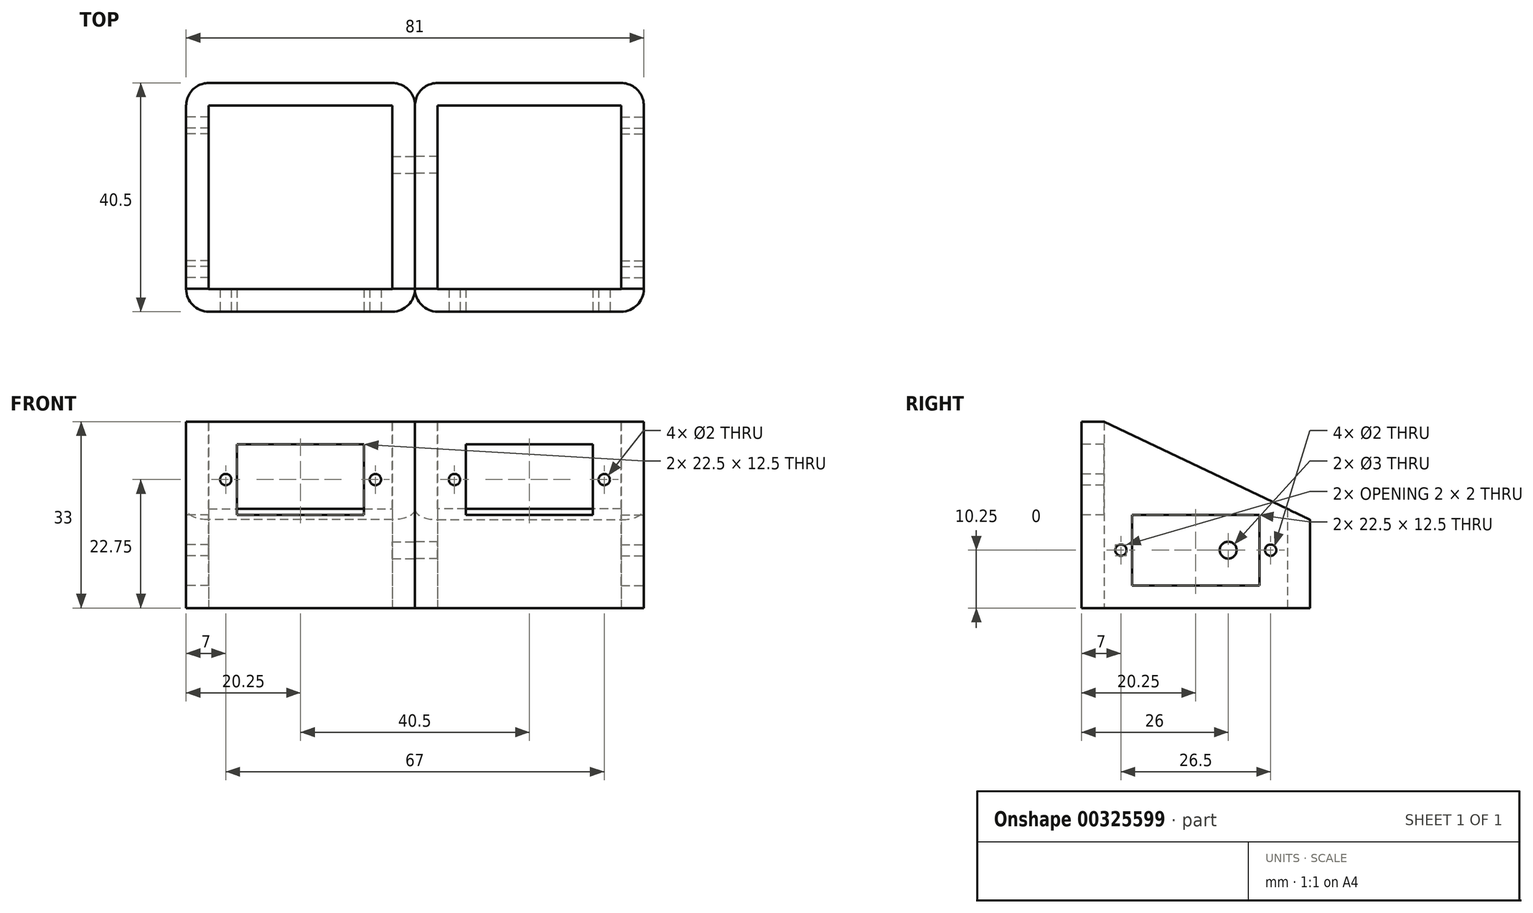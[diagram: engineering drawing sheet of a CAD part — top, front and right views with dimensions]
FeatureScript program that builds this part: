
annotation { "Feature Type Name" : "Feature", "Feature Type Description" : "" }
export const myFeature = defineFeature(function(context is Context, id is Id, definition is map)
    precondition{}
    {
        {
            assignVariable(context, id + "F0", {"name" : "s_w", "anyValue" : 12.5});
        }
        {
            assignVariable(context, id + "F1", {"name" : "size", "anyValue" : 4});
        }
        {
            var Q0;
            Q0=qCreatedBy(makeId("Top.planeOp"),FACE);
            var sketch = newSketch(context, id + "F2", { "sketchPlane" : qUnion([Q0])});
            skLineSegment(sketch, "E0.bottom", {"start": v(-20.25, 20.25) * mm, "end": v(20.25, 20.25) * mm});
            skLineSegment(sketch, "E0.top", {"start": v(-20.25, -20.25) * mm, "end": v(20.25, -20.25) * mm});
            skLineSegment(sketch, "E0.left", {"start": v(-20.25, 20.25) * mm, "end": v(-20.25, -20.25) * mm});
            skLineSegment(sketch, "E0.right", {"start": v(20.25, 20.25) * mm, "end": v(20.25, -20.25) * mm});
            skPoint(sketch, "E1", {"position": v(0, 20.25) * mm});
            skPoint(sketch, "E2", {"position": v(20.25, 0) * mm});
            skLineSegment(sketch, "E3.bottom", {"start": v(-16.25, 16.25) * mm, "end": v(16.25, 16.25) * mm});
            skLineSegment(sketch, "E3.top", {"start": v(-16.25, -16.25) * mm, "end": v(16.25, -16.25) * mm});
            skLineSegment(sketch, "E3.left", {"start": v(-16.25, 16.25) * mm, "end": v(-16.25, -16.25) * mm});
            skLineSegment(sketch, "E3.right", {"start": v(16.25, 16.25) * mm, "end": v(16.25, -16.25) * mm});
            skSolve(sketch);
        }
        {
            var Q0;
            Q0=makeQuery(id+"F2.imprint","IMPRINT",FACE,{"disambiguationData":[TD([[makeQuery(id+"F2.imprint","IMPRINT",EDGE,{"derivedFrom":sQuery(id+"F2.wireOp",EDGE,"E0.bottom")}),-1.0]])]});
            extrude(context, id + "F3", {"entities" : qUnion([Q0]), "depth" : (2 * getVariable(context, 's_w') + 2 * getVariable(context, 'size')) * mm});
        }
        {
            var Q0;
            Q0=makeQuery(id+"F3.opExtrude","SWEPT_FACE",FACE,{"disambiguationData":[OSD([sQuery(id+"F2.wireOp",EDGE,"E0.top")])]});
            var sketch = newSketch(context, id + "F4", { "sketchPlane" : qUnion([Q0])});
            skLineSegment(sketch, "E4.bottom", {"start": v(-11.25, 29) * mm, "end": v(11.25, 29) * mm});
            skLineSegment(sketch, "E4.top", {"start": v(-11.25, 16.5) * mm, "end": v(11.25, 16.5) * mm});
            skLineSegment(sketch, "E4.left", {"start": v(-11.25, 29) * mm, "end": v(-11.25, 16.5) * mm});
            skLineSegment(sketch, "E4.right", {"start": v(11.25, 29) * mm, "end": v(11.25, 16.5) * mm});
            skPoint(sketch, "E5", {"position": v(-11.25, 22.75) * mm});
            skLineSegment(sketch, "E6", {"start": v(-20.25, 22.75) * mm, "end": v(20.25, 22.75) * mm});
            skPoint(sketch, "E7", {"position": v(-13.25, 22.75) * mm});
            skPoint(sketch, "E8", {"position": v(13.25, 22.75) * mm});
            skCircle(sketch, "E9", {"center": v(-13.25, 22.75) * mm, "radius": 1 * mm});
            skCircle(sketch, "E10", {"center": v(13.25, 22.75) * mm, "radius": 1 * mm});
            skSolve(sketch);
        }
        {
            var Q0;
            Q0=makeQuery(id+"F4.imprint","IMPRINT",FACE,{"disambiguationData":[TD([[makeQuery(id+"F4.imprint","IMPRINT",EDGE,{"derivedFrom":sQuery(id+"F4.wireOp",EDGE,"E4.bottom")}),-1.0]])]});
            var Q1;
            {var subQ0=sQuery(id+"F4.wireOp",EDGE,"E4.top");Q1=makeQuery(id+"F4.imprint","IMPRINT",FACE,{"disambiguationData":[TD([[makeQuery(id+"F4.imprint","IMPRINT",EDGE,{"derivedFrom":subQ0}),1.0]])]});}
            var Q2;
            {var subQ0=sQuery(id+"F4.wireOp",EDGE,"E9");var subQ1=sQuery(id+"F4.wireOp",EDGE,"E6");var subQ2=makeQuery(id+"F4.imprint","INTERSECT",VERTEX,{"disambiguationData":[OD(0.0)],"derivedFrom":[subQ1,subQ0]});Q2=makeQuery(id+"F4.imprint","IMPRINT",FACE,{"disambiguationData":[TD([[makeQuery(id+"F4.imprint","IMPRINT",EDGE,{"disambiguationData":[TD([[subQ2,-1.0]])],"derivedFrom":subQ1}),1.0]])]});}
            var Q3;
            {var subQ0=sQuery(id+"F4.wireOp",EDGE,"E9");var subQ1=sQuery(id+"F4.wireOp",EDGE,"E6");var subQ2=makeQuery(id+"F4.imprint","INTERSECT",VERTEX,{"disambiguationData":[OD(0.0)],"derivedFrom":[subQ1,subQ0]});Q3=makeQuery(id+"F4.imprint","IMPRINT",FACE,{"disambiguationData":[TD([[makeQuery(id+"F4.imprint","IMPRINT",EDGE,{"disambiguationData":[TD([[subQ2,-1.0]])],"derivedFrom":subQ1}),-1.0]])]});}
            var Q4;
            {var subQ0=sQuery(id+"F4.wireOp",EDGE,"E10");var subQ1=sQuery(id+"F4.wireOp",EDGE,"E6");var subQ2=makeQuery(id+"F4.imprint","INTERSECT",VERTEX,{"disambiguationData":[OD(0.0)],"derivedFrom":[subQ1,subQ0]});Q4=makeQuery(id+"F4.imprint","IMPRINT",FACE,{"disambiguationData":[TD([[makeQuery(id+"F4.imprint","IMPRINT",EDGE,{"disambiguationData":[TD([[subQ2,-1.0]])],"derivedFrom":subQ1}),1.0]])]});}
            var Q5;
            {var subQ0=sQuery(id+"F4.wireOp",EDGE,"E10");var subQ1=sQuery(id+"F4.wireOp",EDGE,"E6");var subQ2=makeQuery(id+"F4.imprint","INTERSECT",VERTEX,{"disambiguationData":[OD(0.0)],"derivedFrom":[subQ1,subQ0]});Q5=makeQuery(id+"F4.imprint","IMPRINT",FACE,{"disambiguationData":[TD([[makeQuery(id+"F4.imprint","IMPRINT",EDGE,{"disambiguationData":[TD([[subQ2,-1.0]])],"derivedFrom":subQ1}),-1.0]])]});}
            extrude(context, id + "F5", {"entities" : qUnion([Q0, Q1, Q2, Q3, Q4, Q5]), "operationType" : NewBodyOperationType.REMOVE, "oppositeDirection" : true, "depth" : 25 * mm});
        }
        {
            var Q0;
            Q0=makeQuery(id+"F3.opExtrude","SWEPT_FACE",FACE,{"disambiguationData":[OSD([sQuery(id+"F2.wireOp",EDGE,"E0.left")])]});
            var sketch = newSketch(context, id + "F6", { "sketchPlane" : qUnion([Q0])});
            skLineSegment(sketch, "E11.bottom", {"start": v(-11.25, 16.5) * mm, "end": v(11.25, 16.5) * mm});
            skLineSegment(sketch, "E11.top", {"start": v(-11.25, 4) * mm, "end": v(11.25, 4) * mm});
            skLineSegment(sketch, "E11.left", {"start": v(-11.25, 16.5) * mm, "end": v(-11.25, 4) * mm});
            skLineSegment(sketch, "E11.right", {"start": v(11.25, 16.5) * mm, "end": v(11.25, 4) * mm});
            skPoint(sketch, "E12", {"position": v(11.25, 10.25) * mm});
            skLineSegment(sketch, "E13", {"start": v(20.25, 10.25) * mm, "end": v(-20.25, 10.25) * mm});
            skPoint(sketch, "E13.endSnap0", {"position": v(-11.25, 10.25) * mm});
            skPoint(sketch, "E14", {"position": v(13.25, 10.25) * mm});
            skPoint(sketch, "E15", {"position": v(-13.25, 10.25) * mm});
            skCircle(sketch, "E16", {"center": v(13.25, 10.25) * mm, "radius": 1 * mm});
            skCircle(sketch, "E17", {"center": v(-13.25, 10.25) * mm, "radius": 1 * mm});
            skSolve(sketch);
        }
        {
            var Q0;
            Q0=makeQuery(id+"F6.imprint","IMPRINT",FACE,{"disambiguationData":[TD([[makeQuery(id+"F6.imprint","IMPRINT",EDGE,{"derivedFrom":sQuery(id+"F6.wireOp",EDGE,"E11.bottom")}),-1.0]])]});
            var Q1;
            {var subQ0=sQuery(id+"F6.wireOp",EDGE,"E11.top");Q1=makeQuery(id+"F6.imprint","IMPRINT",FACE,{"disambiguationData":[TD([[makeQuery(id+"F6.imprint","IMPRINT",EDGE,{"derivedFrom":subQ0}),1.0]])]});}
            var Q2;
            {var subQ0=sQuery(id+"F6.wireOp",EDGE,"E16");var subQ1=sQuery(id+"F6.wireOp",EDGE,"E13");var subQ2=makeQuery(id+"F6.imprint","INTERSECT",VERTEX,{"disambiguationData":[OD(0.0)],"derivedFrom":[subQ1,subQ0]});Q2=makeQuery(id+"F6.imprint","IMPRINT",FACE,{"disambiguationData":[TD([[makeQuery(id+"F6.imprint","IMPRINT",EDGE,{"disambiguationData":[TD([[subQ2,-1.0]])],"derivedFrom":subQ1}),1.0]])]});}
            var Q3;
            {var subQ0=sQuery(id+"F6.wireOp",EDGE,"E16");var subQ1=sQuery(id+"F6.wireOp",EDGE,"E13");var subQ2=makeQuery(id+"F6.imprint","INTERSECT",VERTEX,{"disambiguationData":[OD(0.0)],"derivedFrom":[subQ1,subQ0]});Q3=makeQuery(id+"F6.imprint","IMPRINT",FACE,{"disambiguationData":[TD([[makeQuery(id+"F6.imprint","IMPRINT",EDGE,{"disambiguationData":[TD([[subQ2,-1.0]])],"derivedFrom":subQ1}),-1.0]])]});}
            var Q4;
            {var subQ0=sQuery(id+"F6.wireOp",EDGE,"E17");var subQ1=sQuery(id+"F6.wireOp",EDGE,"E13");var subQ2=makeQuery(id+"F6.imprint","INTERSECT",VERTEX,{"disambiguationData":[OD(0.0)],"derivedFrom":[subQ1,subQ0]});Q4=makeQuery(id+"F6.imprint","IMPRINT",FACE,{"disambiguationData":[TD([[makeQuery(id+"F6.imprint","IMPRINT",EDGE,{"disambiguationData":[TD([[subQ2,-1.0]])],"derivedFrom":subQ1}),-1.0]])]});}
            var Q5;
            {var subQ0=sQuery(id+"F6.wireOp",EDGE,"E17");var subQ1=sQuery(id+"F6.wireOp",EDGE,"E13");var subQ2=makeQuery(id+"F6.imprint","INTERSECT",VERTEX,{"disambiguationData":[OD(0.0)],"derivedFrom":[subQ1,subQ0]});Q5=makeQuery(id+"F6.imprint","IMPRINT",FACE,{"disambiguationData":[TD([[makeQuery(id+"F6.imprint","IMPRINT",EDGE,{"disambiguationData":[TD([[subQ2,-1.0]])],"derivedFrom":subQ1}),1.0]])]});}
            extrude(context, id + "F7", {"entities" : qUnion([Q0, Q1, Q2, Q3, Q4, Q5]), "operationType" : NewBodyOperationType.REMOVE, "oppositeDirection" : true, "depth" : 25 * mm});
        }
        {
            var Q0;
            Q0=makeQuery(id+"F3.opExtrude","SWEPT_FACE",FACE,{"disambiguationData":[OSD([sQuery(id+"F2.wireOp",EDGE,"E0.right")])]});
            var sketch = newSketch(context, id + "F8", { "sketchPlane" : qUnion([Q0])});
            skLineSegment(sketch, "E18.bottom", {"start": v(-11.25, 16.5) * mm, "end": v(11.25, 16.5) * mm});
            skLineSegment(sketch, "E18.top", {"start": v(-11.25, 4) * mm, "end": v(11.25, 4) * mm});
            skLineSegment(sketch, "E18.left", {"start": v(-11.25, 16.5) * mm, "end": v(-11.25, 4) * mm});
            skLineSegment(sketch, "E18.right", {"start": v(11.25, 16.5) * mm, "end": v(11.25, 4) * mm});
            skPoint(sketch, "E19", {"position": v(11.25, 10.25) * mm});
            skLineSegment(sketch, "E20", {"start": v(11.25, 10.25) * mm, "end": v(-11.25, 10.25) * mm});
            skPoint(sketch, "E21", {"position": v(5.75, 10.25) * mm});
            skCircle(sketch, "E22", {"center": v(5.75, 10.25) * mm, "radius": 1.5 * mm});
            skSolve(sketch);
        }
        {
            var Q0;
            {var subQ0=sQuery(id+"F8.wireOp",EDGE,"E22");var subQ1=sQuery(id+"F8.wireOp",EDGE,"E20");var subQ2=makeQuery(id+"F8.imprint","INTERSECT",VERTEX,{"disambiguationData":[OD(0.0)],"derivedFrom":[subQ1,subQ0]});Q0=makeQuery(id+"F8.imprint","IMPRINT",FACE,{"disambiguationData":[TD([[makeQuery(id+"F8.imprint","IMPRINT",EDGE,{"disambiguationData":[TD([[subQ2,-1.0]])],"derivedFrom":subQ1}),-1.0]])]});}
            var Q1;
            {var subQ0=sQuery(id+"F8.wireOp",EDGE,"E22");var subQ1=sQuery(id+"F8.wireOp",EDGE,"E20");var subQ2=makeQuery(id+"F8.imprint","INTERSECT",VERTEX,{"disambiguationData":[OD(0.0)],"derivedFrom":[subQ1,subQ0]});Q1=makeQuery(id+"F8.imprint","IMPRINT",FACE,{"disambiguationData":[TD([[makeQuery(id+"F8.imprint","IMPRINT",EDGE,{"disambiguationData":[TD([[subQ2,-1.0]])],"derivedFrom":subQ1}),1.0]])]});}
            extrude(context, id + "F9", {"entities" : qUnion([Q0, Q1]), "operationType" : NewBodyOperationType.REMOVE, "oppositeDirection" : true, "depth" : 25 * mm});
        }
        {
            var Q0;
            Q0=makeQuery(id+"F3.opExtrude","SWEPT_FACE",FACE,{"disambiguationData":[OSD([sQuery(id+"F2.wireOp",EDGE,"E0.left")])]});
            var sketch = newSketch(context, id + "F10", { "sketchPlane" : qUnion([Q0])});
            skLineSegment(sketch, "E23", {"start": v(-20.25, 33) * mm, "end": v(16.21, 33) * mm});
            skLineSegment(sketch, "E24", {"start": v(16.21, 33) * mm, "end": v(-20.25, 15.64) * mm});
            skLineSegment(sketch, "E25", {"start": v(-20.25, 15.64) * mm, "end": v(-20.25, 33) * mm});
            skSolve(sketch);
        }
        {
            var Q0;
            Q0=makeQuery(id+"F10.imprint","IMPRINT",FACE,{"disambiguationData":[TD([[makeQuery(id+"F10.imprint","IMPRINT",EDGE,{"derivedFrom":sQuery(id+"F10.wireOp",EDGE,"E23")}),-1.0]])]});
            extrude(context, id + "F11", {"entities" : qUnion([Q0]), "operationType" : NewBodyOperationType.REMOVE, "oppositeDirection" : true, "depth" : 60 * mm});
        }
        {
            var Q0;
            Q0=makeQuery(id+"F3.opExtrude","SWEPT_EDGE",EDGE,{"disambiguationData":[OSD([sQuery(id+"F2.wireOp",EDGE,"E0.top"),sQuery(id+"F2.wireOp",EDGE,"E0.left")])]});
            var Q1;
            Q1=makeQuery(id+"F3.opExtrude","SWEPT_EDGE",EDGE,{"disambiguationData":[OSD([sQuery(id+"F2.wireOp",EDGE,"E0.top"),sQuery(id+"F2.wireOp",EDGE,"E0.right")])]});
            var Q2;
            Q2=makeQuery(id+"F3.opExtrude","SWEPT_EDGE",EDGE,{"disambiguationData":[OSD([sQuery(id+"F2.wireOp",EDGE,"E0.bottom"),sQuery(id+"F2.wireOp",EDGE,"E0.right")])]});
            var Q3;
            Q3=makeQuery(id+"F3.opExtrude","SWEPT_EDGE",EDGE,{"disambiguationData":[OSD([sQuery(id+"F2.wireOp",EDGE,"E0.bottom"),sQuery(id+"F2.wireOp",EDGE,"E0.left")])]});
            fillet(context, id + "F12", {"entities" : qUnion([Q0, Q1, Q2, Q3]), "radius" : (getVariable(context, 'size')) * mm, "tangentPropagation" : true, "allowEdgeOverflow" : false});
        }
        {
            var Q0;
            Q0=makeQuery(id+"F3.opExtrude","SWEPT_BODY",BODY,{"disambiguationData":[OSD([sQuery(id+"F2.wireOp",EDGE,"E0.bottom"),sQuery(id+"F2.wireOp",EDGE,"E0.top"),sQuery(id+"F2.wireOp",EDGE,"E0.left"),sQuery(id+"F2.wireOp",EDGE,"E0.right"),sQuery(id+"F2.wireOp",EDGE,"E3.bottom"),sQuery(id+"F2.wireOp",EDGE,"E3.top"),sQuery(id+"F2.wireOp",EDGE,"E3.left"),sQuery(id+"F2.wireOp",EDGE,"E3.right")])]});
            var Q1;
            Q1=qCreatedBy(makeId("Top.planeOp"),FACE);
            mirror(context, id + "F13", {"entities" : qUnion([Q0]), "mirrorPlane" : qUnion([Q1])});
        }
        {
            var Q0;
            Q0=makeQuery(id+"F13.opPattern","COPY",BODY,{"derivedFrom":makeQuery(id+"F3.opExtrude","SWEPT_BODY",BODY,{"disambiguationData":[OSD([sQuery(id+"F2.wireOp",EDGE,"E0.bottom"),sQuery(id+"F2.wireOp",EDGE,"E0.top"),sQuery(id+"F2.wireOp",EDGE,"E0.left"),sQuery(id+"F2.wireOp",EDGE,"E0.right"),sQuery(id+"F2.wireOp",EDGE,"E3.bottom"),sQuery(id+"F2.wireOp",EDGE,"E3.top"),sQuery(id+"F2.wireOp",EDGE,"E3.left"),sQuery(id+"F2.wireOp",EDGE,"E3.right")])]}),"instanceName":"1"});
            var Q1;
            Q1=makeQuery(id+"F13.opPattern","COPY",EDGE,{"derivedFrom":makeQuery(id+"F3.opExtrude","CAP_EDGE",EDGE,{"disambiguationData":[OSD([sQuery(id+"F2.wireOp",EDGE,"E0.right")])],"isStart":true}),"instanceName":"1"});
            transform(context, id + "F14", {"entities" : qUnion([Q0]), "transformType" : TransformType.ROTATION, "transformAxis" : qUnion([Q1]), "angle" : 180 * degree, "makeCopy" : false});
        }
    });
